# Revit family: НЕВАТОМ_Зонт VO, Версия 1
name_source: partatom
category: Арматура воздуховодов
revit_build: Autodesk Revit 2017 (Build: 20170118_1100(x64)
units: mm (PartAtom-declared; Revit-internal decimal feet)

## family parameters
Всегда вертикально = Да
На основе рабочей плоскости = Нет
Общий = Нет
При загрузке вырезать с полостями = Нет
Размер круглого соединителя = Использовать диаметр
Тип детали = Присоединяется

## types (8) — shared parameters
ADSK_Единица измерения = шт.
ADSK_Завод-изготовитель = НЕВАТОМ
ADSK_Наименование = Зонт
DDD = 934 мм
Nevatom_URL = https://t.me
d5 = 577 мм
видимость ножки 6 = Да
высота зонта = 200 мм
высота кольца = 10 мм
высота ободка = 20 мм
толщина зонта = 4 мм

## per-type parameters (varying)
| type | ADSK_Марка | ADSK_Масса | ADSK_Материал наименование | D | D2 | DDDD | Db1 | H | L | L1 | h | видимость ножки | видимость ножки 2 | видимость ножки 3 | видимость ножки 4 | видимость ножки 5 | видимость ножки 7 | видимость ножки 8 | видимость ножки 9 | высота ножек |
| Зонт VO №4,5 | VO №4,5 | 20.2 | оцинкованная сталь | 560 мм | 610 мм | 273 мм | 282 мм | 261 мм | 925 мм | 640 мм | 222 мм | Нет | Да | Да | Нет | Да | Нет | Нет | Да | 221 мм |
| Зонт VO №4 | VO №4 | 17.3 | оцинкованная сталь | 500 мм | 550 мм | 243 мм | 252 мм | 233 мм | 823 мм | 600 мм | 193 мм | Да | Да | Да | Нет | Да | Нет | Нет | Нет | 193 мм |
| Зонт VO №5 | VO №5 | 25 |  | 630 мм | 680 мм | 308 мм | 317 мм | 285 мм | 1048 мм | 720 мм | 259 мм | Нет | Да | Да | Нет | Нет | Да | Да | Да | 221 мм |
| Зонт VO №9 | VO №9 | 72.4 |  | 1120 мм | 1184 мм | 553 мм | 562 мм | 509 мм | 1986 мм | 1212 мм | 453 мм | Да | Да | Да | Да | Да | Да | Да | Да | 469 мм |
| Зонт VO №8 | VO №8 | 60 |  | 1000 мм | 1080 мм | 493 мм | 502 мм | 455 мм | 1602 мм | 1212 мм | 426 мм | Нет | Да | Да | Да | Да | Да | Да | Да | 415 мм |
| Зонт VO №7,1 | VO №7,1 | 49.2 | сталь оцинкованная | 900 мм | 964 мм | 443 мм | 452 мм | 409 мм | 1484 мм | 1000 мм | 361 мм | Нет | Да | Да | Да | Да | Да | Да | Да | 415 мм |
| ЗОНТ VO №6,3 | VO №6,3 | 36.3 | сталь оцинкованная | 800 мм | 864 мм | 393 мм | 402 мм | 355 мм | 1319 мм | 904 мм | 361 мм | Нет | Нет | Нет | Нет | Да | Да | Да | Да | 415 мм |
| Зонт VO №5,6 | VO №5,6 | 31.8 | сталь оцинкованная | 710 мм | 790 мм | 348 мм | 357 мм | 320 мм | 1270 мм | 824 мм | 277 мм | Нет | Нет | Нет | Нет | Да | Да | Да | Да | 415 мм |
